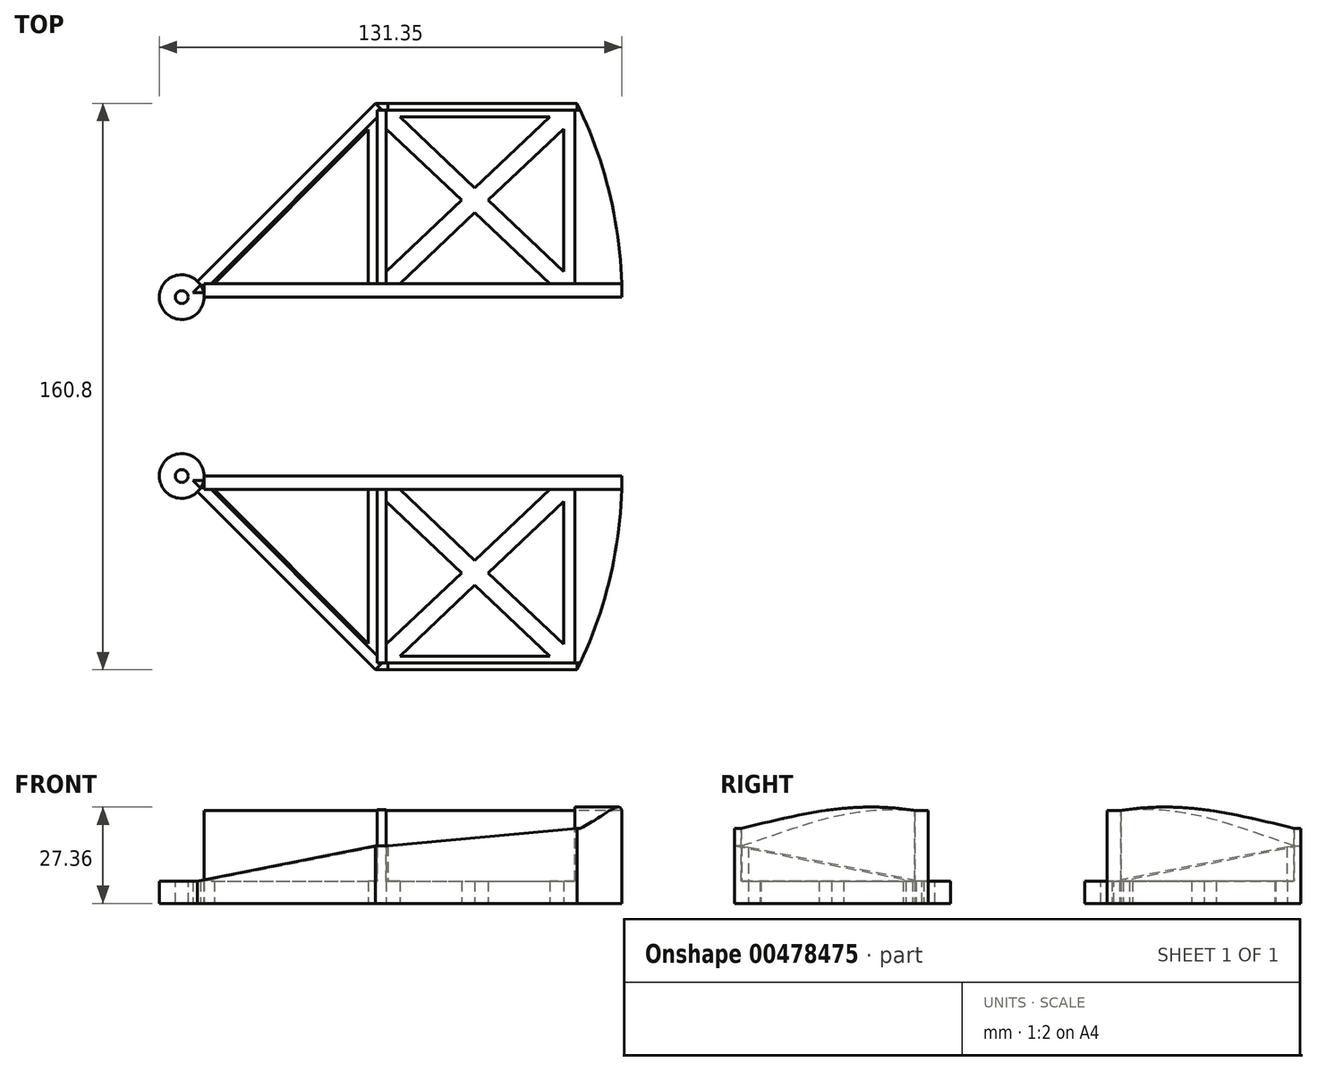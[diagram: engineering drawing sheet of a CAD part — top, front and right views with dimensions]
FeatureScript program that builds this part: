
annotation { "Feature Type Name" : "Feature", "Feature Type Description" : "" }
export const myFeature = defineFeature(function(context is Context, id is Id, definition is map)
    precondition{}
    {
        {
            var Q0;
            Q0=qCreatedBy(makeId("Top.planeOp"),FACE);
            var sketch = newSketch(context, id + "F0", { "sketchPlane" : qUnion([Q0])});
            skLineSegment(sketch, "E0", {"start": v(0, 0) * mm, "end": v(55, 55) * mm});
            skLineSegment(sketch, "E1", {"start": v(55, 55) * mm, "end": v(112.25, 55) * mm});
            skLineSegment(sketch, "E2", {"start": v(112.25, 55) * mm, "end": v(112.25, 0) * mm});
            skLineSegment(sketch, "E3", {"start": v(112.25, 0) * mm, "end": v(0, 0) * mm});
            skLineSegment(sketch, "E4.0", {"start": v(3.14, 1.3) * mm, "end": v(55.54, 53.7) * mm});
            skLineSegment(sketch, "E4.1", {"start": v(110.95, 1.3) * mm, "end": v(3.14, 1.3) * mm});
            skLineSegment(sketch, "E4.2", {"start": v(110.95, 53.7) * mm, "end": v(110.95, 1.3) * mm});
            skLineSegment(sketch, "E4.3", {"start": v(55.54, 53.7) * mm, "end": v(110.95, 53.7) * mm});
            skLineSegment(sketch, "E5", {"start": v(55.54, 53.7) * mm, "end": v(83.24, 27.5) * mm});
            skLineSegment(sketch, "E6", {"start": v(55.54, 53.7) * mm, "end": v(55.54, 1.3) * mm});
            skLineSegment(sketch, "E7", {"start": v(83.24, 27.5) * mm, "end": v(110.95, 1.3) * mm});
            skLineSegment(sketch, "E8", {"start": v(55.54, 1.3) * mm, "end": v(83.24, 27.5) * mm});
            skLineSegment(sketch, "E9", {"start": v(83.24, 27.5) * mm, "end": v(110.95, 53.7) * mm});
            skLineSegment(sketch, "E10.0", {"start": v(58.08, 47.8) * mm, "end": v(58.08, 7.2) * mm});
            skLineSegment(sketch, "E10.1", {"start": v(58.08, 47.8) * mm, "end": v(79.55, 27.5) * mm});
            skLineSegment(sketch, "E10.2", {"start": v(58.08, 7.2) * mm, "end": v(79.55, 27.5) * mm});
            skLineSegment(sketch, "E11.0", {"start": v(61.92, 51.16) * mm, "end": v(83.24, 31) * mm});
            skLineSegment(sketch, "E11.1", {"start": v(61.92, 51.16) * mm, "end": v(104.57, 51.16) * mm});
            skLineSegment(sketch, "E11.2", {"start": v(83.24, 31) * mm, "end": v(104.57, 51.16) * mm});
            skLineSegment(sketch, "E12.0", {"start": v(86.94, 27.5) * mm, "end": v(108.4, 7.2) * mm});
            skLineSegment(sketch, "E12.1", {"start": v(86.94, 27.5) * mm, "end": v(108.4, 47.8) * mm});
            skLineSegment(sketch, "E12.2", {"start": v(108.4, 47.8) * mm, "end": v(108.4, 7.2) * mm});
            skLineSegment(sketch, "E13", {"start": v(61.92, 3.84) * mm, "end": v(83.24, 24) * mm});
            skLineSegment(sketch, "E14", {"start": v(83.24, 24) * mm, "end": v(104.57, 3.84) * mm});
            skLineSegment(sketch, "E15", {"start": v(104.57, 3.84) * mm, "end": v(61.92, 3.84) * mm});
            skLineSegment(sketch, "E16", {"start": v(9.27, 3.84) * mm, "end": v(53, 47.57) * mm});
            skLineSegment(sketch, "E17", {"start": v(53, 47.57) * mm, "end": v(53, 3.84) * mm});
            skLineSegment(sketch, "E18", {"start": v(53, 3.84) * mm, "end": v(9.27, 3.84) * mm});
            skCircle(sketch, "E19", {"center": v(0, 0) * mm, "radius": 6.35 * mm});
            skCircle(sketch, "E20", {"center": v(0, 0) * mm, "radius": 125 * mm});
            skLineSegment(sketch, "E21", {"start": v(112.25, 0) * mm, "end": v(125, 0) * mm});
            skSolve(sketch);
        }
        {
            var Q0;
            {var subQ0=sQuery(id+"F0.wireOp",EDGE,"E3");var subQ1=sQuery(id+"F0.wireOp",EDGE,"E0");var subQ2=makeQuery(id+"F0.imprint","INTERSECT",VERTEX,{"derivedFrom":[subQ1,subQ0]});Q0=makeQuery(id+"F0.imprint","IMPRINT",FACE,{"disambiguationData":[TD([[makeQuery(id+"F0.imprint","IMPRINT",EDGE,{"disambiguationData":[TD([[subQ2,-1.0]])],"derivedFrom":subQ1}),1.0]])]});}
            var Q1;
            {var subQ6=sQuery(id+"F0.wireOp",EDGE,"E3");var subQ7=sQuery(id+"F0.wireOp",EDGE,"E0");var subQ8=makeQuery(id+"F0.imprint","INTERSECT",VERTEX,{"derivedFrom":[subQ7,subQ6]});Q1=makeQuery(id+"F0.imprint","IMPRINT",FACE,{"disambiguationData":[TD([[makeQuery(id+"F0.imprint","IMPRINT",EDGE,{"disambiguationData":[TD([[subQ8,-1.0]])],"derivedFrom":subQ7}),-1.0]])]});}
            var Q2;
            {var subQ13=sQuery(id+"F0.wireOp",EDGE,"E1");Q2=makeQuery(id+"F0.imprint","IMPRINT",FACE,{"disambiguationData":[TD([[makeQuery(id+"F0.imprint","IMPRINT",EDGE,{"derivedFrom":subQ13}),-1.0]])]});}
            var Q3;
            {var subQ0=sQuery(id+"F0.wireOp",EDGE,"E6");Q3=makeQuery(id+"F0.imprint","IMPRINT",FACE,{"disambiguationData":[TD([[makeQuery(id+"F0.imprint","IMPRINT",EDGE,{"derivedFrom":subQ0}),-1.0]])]});}
            var Q4;
            Q4=makeQuery(id+"F0.imprint","IMPRINT",FACE,{"disambiguationData":[TD([[makeQuery(id+"F0.imprint","IMPRINT",EDGE,{"derivedFrom":sQuery(id+"F0.wireOp",EDGE,"E5")}),-1.0]])]});
            var Q5;
            {var subQ1=sQuery(id+"F0.wireOp",EDGE,"E7");Q5=makeQuery(id+"F0.imprint","IMPRINT",FACE,{"disambiguationData":[TD([[makeQuery(id+"F0.imprint","IMPRINT",EDGE,{"derivedFrom":subQ1}),-1.0]])]});}
            var Q6;
            Q6=makeQuery(id+"F0.imprint","IMPRINT",FACE,{"disambiguationData":[TD([[makeQuery(id+"F0.imprint","IMPRINT",EDGE,{"derivedFrom":sQuery(id+"F0.wireOp",EDGE,"E4.3")}),-1.0]])]});
            var Q7;
            Q7=makeQuery(id+"F0.imprint","IMPRINT",FACE,{"disambiguationData":[TD([[makeQuery(id+"F0.imprint","IMPRINT",EDGE,{"derivedFrom":sQuery(id+"F0.wireOp",EDGE,"E4.2")}),-1.0]])]});
            var Q8;
            {var subQ0=sQuery(id+"F0.wireOp",EDGE,"E2");Q8=makeQuery(id+"F0.imprint","IMPRINT",FACE,{"disambiguationData":[TD([[makeQuery(id+"F0.imprint","IMPRINT",EDGE,{"derivedFrom":subQ0}),1.0]])]});}
            extrude(context, id + "F1", {"entities" : qUnion([Q0, Q1, Q2, Q3, Q4, Q5, Q6, Q7, Q8]), "depth" : 6.35 * mm});
        }
        {
            var Q0;
            Q0=makeQuery(id+"F1.opExtrude","CAP_FACE",FACE,{"disambiguationData":[OSD([sQuery(id+"F0.wireOp",EDGE,"E0"),sQuery(id+"F0.wireOp",EDGE,"E1"),sQuery(id+"F0.wireOp",EDGE,"E2"),sQuery(id+"F0.wireOp",EDGE,"E3"),sQuery(id+"F0.wireOp",EDGE,"E10.0"),sQuery(id+"F0.wireOp",EDGE,"E10.1"),sQuery(id+"F0.wireOp",EDGE,"E10.2"),sQuery(id+"F0.wireOp",EDGE,"E11.0"),sQuery(id+"F0.wireOp",EDGE,"E11.1"),sQuery(id+"F0.wireOp",EDGE,"E11.2"),sQuery(id+"F0.wireOp",EDGE,"E12.0"),sQuery(id+"F0.wireOp",EDGE,"E12.1"),sQuery(id+"F0.wireOp",EDGE,"E12.2"),sQuery(id+"F0.wireOp",EDGE,"E13"),sQuery(id+"F0.wireOp",EDGE,"E14"),sQuery(id+"F0.wireOp",EDGE,"E15"),sQuery(id+"F0.wireOp",EDGE,"E16"),sQuery(id+"F0.wireOp",EDGE,"E17"),sQuery(id+"F0.wireOp",EDGE,"E18"),sQuery(id+"F0.wireOp",EDGE,"E19")])],"isStart":false});
            var sketch = newSketch(context, id + "F2", { "sketchPlane" : qUnion([Q0])});
            skCircle(sketch, "E22", {"center": v(0, 0) * mm, "radius": 1.84 * mm});
            skSolve(sketch);
        }
        {
            var Q0;
            Q0=qSketchRegion(id+"F2",true);
            extrude(context, id + "F3", {"entities" : qUnion([Q0]), "operationType" : NewBodyOperationType.REMOVE, "oppositeDirection" : true, "depth" : 25.4 * mm});
        }
        {
            var Q0;
            Q0=makeQuery(id+"F1.opExtrude","CAP_FACE",FACE,{"disambiguationData":[OSD([sQuery(id+"F0.wireOp",EDGE,"E0"),sQuery(id+"F0.wireOp",EDGE,"E1"),sQuery(id+"F0.wireOp",EDGE,"E2"),sQuery(id+"F0.wireOp",EDGE,"E3"),sQuery(id+"F0.wireOp",EDGE,"E10.0"),sQuery(id+"F0.wireOp",EDGE,"E10.1"),sQuery(id+"F0.wireOp",EDGE,"E10.2"),sQuery(id+"F0.wireOp",EDGE,"E11.0"),sQuery(id+"F0.wireOp",EDGE,"E11.1"),sQuery(id+"F0.wireOp",EDGE,"E11.2"),sQuery(id+"F0.wireOp",EDGE,"E12.0"),sQuery(id+"F0.wireOp",EDGE,"E12.1"),sQuery(id+"F0.wireOp",EDGE,"E12.2"),sQuery(id+"F0.wireOp",EDGE,"E13"),sQuery(id+"F0.wireOp",EDGE,"E14"),sQuery(id+"F0.wireOp",EDGE,"E15"),sQuery(id+"F0.wireOp",EDGE,"E16"),sQuery(id+"F0.wireOp",EDGE,"E17"),sQuery(id+"F0.wireOp",EDGE,"E18"),sQuery(id+"F0.wireOp",EDGE,"E19")])],"isStart":false});
            var sketch = newSketch(context, id + "F4", { "sketchPlane" : qUnion([Q0])});
            skLineSegment(sketch, "E23.bottom", {"start": v(9.27, 0) * mm, "end": v(6.35, 0) * mm});
            skLineSegment(sketch, "E23.top", {"start": v(9.27, 3.84) * mm, "end": v(6.35, 3.84) * mm});
            skLineSegment(sketch, "E23.left", {"start": v(6.35, 0) * mm, "end": v(6.35, 3.84) * mm});
            skLineSegment(sketch, "E23.right", {"start": v(9.27, 0) * mm, "end": v(9.27, 3.84) * mm});
            skSolve(sketch);
        }
        {
            var Q0;
            Q0=qSketchRegion(id+"F4",true);
            extrude(context, id + "F5", {"entities" : qUnion([Q0]), "operationType" : NewBodyOperationType.ADD, "depth" : 20 * mm});
        }
        {
            var Q0;
            Q0=makeQuery(id+"F1.opExtrude","SWEPT_FACE",FACE,{"disambiguationData":[OSD([sQuery(id+"F0.wireOp",EDGE,"E0")])]});
            var sketch = newSketch(context, id + "F6", { "sketchPlane" : qUnion([Q0])});
            skLineSegment(sketch, "E24", {"start": v(-77.78, 6.35) * mm, "end": v(-77.78, 16.35) * mm});
            skLineSegment(sketch, "E25", {"start": v(-77.78, 16.35) * mm, "end": v(-6.35, 6.35) * mm});
            skLineSegment(sketch, "E26", {"start": v(-6.35, 6.35) * mm, "end": v(-77.78, 6.35) * mm});
            skSolve(sketch);
        }
        {
            var Q0;
            Q0=qSketchRegion(id+"F6",true);
            var Q1;
            Q1=makeQuery(id+"F1.opExtrude","SWEPT_FACE",FACE,{"disambiguationData":[OSD([sQuery(id+"F0.wireOp",EDGE,"E16")])]});
            extrude(context, id + "F7", {"entities" : qUnion([Q0]), "operationType" : NewBodyOperationType.ADD, "oppositeDirection" : true, "endBoundEntityFace" : qUnion([Q1]), "depth" : 3.17 * mm});
        }
        {
            var Q0;
            Q0=makeQuery(id+"F1.opExtrude","SWEPT_FACE",FACE,{"disambiguationData":[OSD([sQuery(id+"F0.wireOp",EDGE,"E1")])]});
            var sketch = newSketch(context, id + "F8", { "sketchPlane" : qUnion([Q0])});
            skLineSegment(sketch, "E27", {"start": v(-112.25, 6.35) * mm, "end": v(-112.25, 21.35) * mm});
            skLineSegment(sketch, "E28", {"start": v(-112.25, 21.35) * mm, "end": v(-58.52, 16.35) * mm});
            skLineSegment(sketch, "E29", {"start": v(-58.52, 16.35) * mm, "end": v(-58.52, 6.35) * mm});
            skSolve(sketch);
        }
        {
            var Q0;
            {var subQ0=sQuery(id+"F8.wireOp",EDGE,"E27");Q0=makeQuery(id+"F8.imprint","IMPRINT",FACE,{"disambiguationData":[TD([[makeQuery(id+"F8.imprint","IMPRINT",EDGE,{"derivedFrom":subQ0}),-1.0]])]});}
            extrude(context, id + "F9", {"entities" : qUnion([Q0]), "operationType" : NewBodyOperationType.ADD, "oppositeDirection" : true, "depth" : 1.9 * mm});
        }
        {
            var Q1;
            Q1=makeQuery(id+"F7.opExtrude","SWEPT_FACE",FACE,{"disambiguationData":[OSD([sQuery(id+"F6.wireOp",EDGE,"E24")])]});
            var Q2;
            Q2=makeQuery(id+"F9.opExtrude","SWEPT_FACE",FACE,{"disambiguationData":[OSD([sQuery(id+"F8.wireOp",EDGE,"E29")])]});
            loft(context, id + "F10", {"operationType" : NewBodyOperationType.ADD, "sheetProfilesArray" : [{ "sheetProfileEntities" : qUnion([Q1]) }, { "sheetProfileEntities" : qUnion([Q2]) }]});
        }
        {
            var Q0;
            Q0=makeQuery(id+"F1.opExtrude","SWEPT_FACE",FACE,{"disambiguationData":[OSD([sQuery(id+"F0.wireOp",EDGE,"E10.0")])]});
            var sketch = newSketch(context, id + "F11", { "sketchPlane" : qUnion([Q0])});
            skLineSegment(sketch, "E30.0.0", {"start": v(0, 24.38) * mm, "end": v(0, 6.35) * mm});
            skFitSpline(sketch, "E30.0.1", {"points": [v(0, 24.38) * mm, v(1.99, 25.62) * mm, v(2.56, 26) * mm, v(3.84, 26.35) * mm]});
            skLineSegment(sketch, "E30.0.2", {"start": v(3.84, 6.35) * mm, "end": v(3.84, 26.35) * mm});
            skLineSegment(sketch, "E30.0.3", {"start": v(0, 6.35) * mm, "end": v(3.84, 6.35) * mm});
            skLineSegment(sketch, "E31.0.0", {"start": v(53.1, 21.18) * mm, "end": v(53.1, 21.35) * mm});
            skLineSegment(sketch, "E31.0.3", {"start": v(55, 16.35) * mm, "end": v(53.1, 16.35) * mm});
            skLineSegment(sketch, "E31.0.4", {"start": v(53.1, 16.35) * mm, "end": v(53.1, 21.18) * mm});
            skLineSegment(sketch, "E32", {"start": v(53.1, 16.35) * mm, "end": v(53.1, 6.35) * mm});
            skLineSegment(sketch, "E33", {"start": v(3.84, 6.35) * mm, "end": v(53.1, 6.35) * mm});
            skFitSpline(sketch, "E34", {"points": [v(53.1, 16.35) * mm, v(3.84, 26.35) * mm], "startDerivative": vector(-52.9, 16.95) * mm, "endDerivative": vector(-57.88, -5.03) * mm});
            skSolve(sketch);
        }
        {
            var Q0;
            {var subQ0=sQuery(id+"F11.wireOp",EDGE,"E32");Q0=makeQuery(id+"F11.imprint","IMPRINT",FACE,{"disambiguationData":[TD([[makeQuery(id+"F11.imprint","IMPRINT",EDGE,{"derivedFrom":subQ0}),-1.0]])]});}
            extrude(context, id + "F12", {"entities" : qUnion([Q0]), "operationType" : NewBodyOperationType.ADD, "oppositeDirection" : true, "depth" : 2.54 * mm});
        }
        {
            var Q0;
            Q0=makeQuery(id+"F5.boolean.opBoolean","MERGE",FACE,{"derivedFrom":[makeQuery(id+"F1.opExtrude","SWEPT_FACE",FACE,{"disambiguationData":[OSD([sQuery(id+"F0.wireOp",EDGE,"E3")])]}),makeQuery(id+"F5.opExtrude","SWEPT_FACE",FACE,{"disambiguationData":[OSD([sQuery(id+"F4.wireOp",EDGE,"E23.bottom")])]})]});
            cPlane(context, id + "F13", {"entities" : qUnion([Q0]), "cplaneType" : CPlaneType.OFFSET, "offset" : 25.4 * mm, "width" : 152.4 * mm, "height" : 152.4 * mm});
        }
        {
            var Q0;
            Q0=makeQuery(id+"F1.opExtrude","SWEPT_BODY",BODY,{"disambiguationData":[OSD([sQuery(id+"F0.wireOp",EDGE,"E0"),sQuery(id+"F0.wireOp",EDGE,"E1"),sQuery(id+"F0.wireOp",EDGE,"E2"),sQuery(id+"F0.wireOp",EDGE,"E3"),sQuery(id+"F0.wireOp",EDGE,"E10.0"),sQuery(id+"F0.wireOp",EDGE,"E10.1"),sQuery(id+"F0.wireOp",EDGE,"E10.2"),sQuery(id+"F0.wireOp",EDGE,"E11.0"),sQuery(id+"F0.wireOp",EDGE,"E11.1"),sQuery(id+"F0.wireOp",EDGE,"E11.2"),sQuery(id+"F0.wireOp",EDGE,"E12.0"),sQuery(id+"F0.wireOp",EDGE,"E12.1"),sQuery(id+"F0.wireOp",EDGE,"E12.2"),sQuery(id+"F0.wireOp",EDGE,"E13"),sQuery(id+"F0.wireOp",EDGE,"E14"),sQuery(id+"F0.wireOp",EDGE,"E15"),sQuery(id+"F0.wireOp",EDGE,"E16"),sQuery(id+"F0.wireOp",EDGE,"E17"),sQuery(id+"F0.wireOp",EDGE,"E18"),sQuery(id+"F0.wireOp",EDGE,"E19")])]});
            var Q1;
            Q1=qCreatedBy(id+"F13.planeOp",FACE);
            mirror(context, id + "F14", {"entities" : qUnion([Q0]), "mirrorPlane" : qUnion([Q1])});
        }
        {
            var Q0;
            Q0=makeQuery(id+"F5.opExtrude","SWEPT_FACE",FACE,{"disambiguationData":[OSD([sQuery(id+"F4.wireOp",EDGE,"E23.right")])]});
            var sketch = newSketch(context, id + "F15", { "sketchPlane" : qUnion([Q0])});
            skPoint(sketch, "E35.0", {"position": v(0, 26.35) * mm});
            skLineSegment(sketch, "E36.bottom", {"start": v(0, 26.35) * mm, "end": v(3.84, 26.35) * mm});
            skLineSegment(sketch, "E36.top", {"start": v(0, 6.35) * mm, "end": v(3.84, 6.35) * mm});
            skLineSegment(sketch, "E36.left", {"start": v(0, 26.35) * mm, "end": v(0, 6.35) * mm});
            skLineSegment(sketch, "E36.right", {"start": v(3.84, 26.35) * mm, "end": v(3.84, 6.35) * mm});
            skSolve(sketch);
        }
        {
            var Q0;
            Q0=qSketchRegion(id+"F15",true);
            var Q1;
            Q1=makeQuery(id+"F1.opExtrude","SWEPT_FACE",FACE,{"disambiguationData":[OSD([sQuery(id+"F0.wireOp",EDGE,"E20")])]});
            extrude(context, id + "F16", {"entities" : qUnion([Q0]), "operationType" : NewBodyOperationType.ADD, "endBound" : BoundingType.UP_TO_SURFACE, "endBoundEntityFace" : qUnion([Q1]), "depth" : 25.4 * mm});
        }
        {
            var Q0;
            {var subQ0=sQuery(id+"F0.wireOp",EDGE,"E20");var subQ1=sQuery(id+"F0.wireOp",EDGE,"E18");var subQ2=sQuery(id+"F0.wireOp",EDGE,"E17");var subQ3=sQuery(id+"F0.wireOp",EDGE,"E16");var subQ4=sQuery(id+"F0.wireOp",EDGE,"E15");var subQ5=sQuery(id+"F0.wireOp",EDGE,"E14");var subQ6=sQuery(id+"F0.wireOp",EDGE,"E13");var subQ7=sQuery(id+"F0.wireOp",EDGE,"E12.2");var subQ8=sQuery(id+"F0.wireOp",EDGE,"E12.1");var subQ9=sQuery(id+"F0.wireOp",EDGE,"E10.0");var subQ10=sQuery(id+"F0.wireOp",EDGE,"E21");var subQ11=sQuery(id+"F0.wireOp",EDGE,"E3");var subQ12=sQuery(id+"F0.wireOp",EDGE,"E1");var subQ13=sQuery(id+"F0.wireOp",EDGE,"E0");var subQ14=sQuery(id+"F0.wireOp",EDGE,"E11.1");var subQ15=sQuery(id+"F0.wireOp",EDGE,"E10.1");var subQ16=sQuery(id+"F0.wireOp",EDGE,"E10.2");var subQ17=sQuery(id+"F0.wireOp",EDGE,"E11.0");var subQ18=sQuery(id+"F0.wireOp",EDGE,"E11.2");var subQ19=sQuery(id+"F0.wireOp",EDGE,"E12.0");Q0=makeQuery(id+"F14.opPattern","COPY",FACE,{"derivedFrom":makeQuery(id+"F7.boolean.opBoolean","SPLIT",FACE,{"disambiguationData":[TD([makeQuery(id+"F1.opExtrude","SWEPT_FACE",FACE,{"disambiguationData":[OSD([subQ12])]})])],"derivedFrom":makeQuery(id+"F1.opExtrude","CAP_FACE",FACE,{"disambiguationData":[OSD([subQ13,subQ12,subQ11,sQuery(id+"F0.wireOp",EDGE,"E4.0"),sQuery(id+"F0.wireOp",EDGE,"E4.1"),subQ9,subQ15,subQ16,subQ17,subQ14,subQ18,subQ19,subQ8,subQ7,subQ6,subQ5,subQ4,subQ3,subQ2,subQ1,sQuery(id+"F0.wireOp",EDGE,"E19"),subQ0,subQ10])],"isStart":false})}),"instanceName":"1"});}
            var sketch = newSketch(context, id + "F17", { "sketchPlane" : qUnion([Q0])});
            skLineSegment(sketch, "E37", {"start": v(112.25, -103.9) * mm, "end": v(113.16, -103.9) * mm});
            skLineSegment(sketch, "E38.0.0", {"start": v(58.08, -54.64) * mm, "end": v(58.08, -58) * mm});
            skLineSegment(sketch, "E38.0.1", {"start": v(58.08, -58) * mm, "end": v(79.55, -78.3) * mm});
            skLineSegment(sketch, "E38.0.2", {"start": v(79.55, -78.3) * mm, "end": v(58.08, -98.6) * mm});
            skLineSegment(sketch, "E38.0.3", {"start": v(58.08, -98.6) * mm, "end": v(58.08, -103.78) * mm});
            skLineSegment(sketch, "E38.0.4", {"start": v(58.08, -103.78) * mm, "end": v(58.52, -103.9) * mm});
            skLineSegment(sketch, "E38.0.5", {"start": v(58.52, -103.9) * mm, "end": v(112.25, -103.9) * mm});
            skLineSegment(sketch, "E38.0.6", {"start": v(112.25, -103.9) * mm, "end": v(112.25, -105.8) * mm});
            skArc(sketch, "E38.0.7", {"start": v(112.25, -105.8) * mm, "mid": v(121.77, -79.03) * mm, "end": v(125, -50.8) * mm});
            skLineSegment(sketch, "E38.0.8", {"start": v(125, -50.8) * mm, "end": v(9.27, -50.8) * mm});
            skLineSegment(sketch, "E38.0.9", {"start": v(9.27, -50.8) * mm, "end": v(9.27, -54.64) * mm});
            skLineSegment(sketch, "E38.0.10", {"start": v(9.27, -54.64) * mm, "end": v(53, -54.64) * mm});
            skLineSegment(sketch, "E38.0.11", {"start": v(53, -54.64) * mm, "end": v(53, -98.37) * mm});
            skLineSegment(sketch, "E38.0.12", {"start": v(53, -98.37) * mm, "end": v(9.27, -54.64) * mm});
            skLineSegment(sketch, "E38.0.13", {"start": v(9.27, -54.64) * mm, "end": v(8.33, -54.64) * mm});
            skLineSegment(sketch, "E38.0.14", {"start": v(8.33, -54.64) * mm, "end": v(55.54, -101.85) * mm});
            skLineSegment(sketch, "E38.0.15", {"start": v(55.54, -101.85) * mm, "end": v(55.54, -54.64) * mm});
            skLineSegment(sketch, "E38.0.16", {"start": v(55.54, -54.64) * mm, "end": v(58.08, -54.64) * mm});
            skSolve(sketch);
        }
        {
            var Q0;
            {var subQ0=sQuery(id+"F17.wireOp",EDGE,"E37");Q0=makeQuery(id+"F17.imprint","IMPRINT",FACE,{"disambiguationData":[TD([[makeQuery(id+"F17.imprint","IMPRINT",EDGE,{"derivedFrom":subQ0}),-1.0]])]});}
            var Q1;
            Q1=makeQuery(id+"F14.opPattern","COPY",VERTEX,{"derivedFrom":makeQuery(id+"F9.opExtrude","CAP_VERTEX",VERTEX,{"disambiguationData":[OSD([sQuery(id+"F8.wireOp",EDGE,"E27"),sQuery(id+"F8.wireOp",EDGE,"E28")])],"isStart":true}),"instanceName":"1"});
            extrude(context, id + "F18", {"entities" : qUnion([Q0]), "operationType" : NewBodyOperationType.ADD, "endBound" : BoundingType.UP_TO_VERTEX, "endBoundEntityVertex" : qUnion([Q1]), "depth" : 25.4 * mm});
        }
        {
            var Q0;
            Q0=makeQuery(id+"F14.opPattern","COPY",FACE,{"derivedFrom":makeQuery(id+"F1.opExtrude","SWEPT_FACE",FACE,{"disambiguationData":[OSD([sQuery(id+"F0.wireOp",EDGE,"E12.2")])]}),"instanceName":"1"});
            cPlane(context, id + "F19", {"entities" : qUnion([Q0]), "cplaneType" : CPlaneType.OFFSET, "offset" : 3.17 * mm, "oppositeDirection" : true, "width" : 152.4 * mm, "height" : 152.4 * mm});
        }
        {
            var Q0;
            Q0=qCreatedBy(id+"F19.planeOp",FACE);
            var sketch = newSketch(context, id + "F20", { "sketchPlane" : qUnion([Q0])});
            skLineSegment(sketch, "E39.0.0", {"start": v(105.8, 0) * mm, "end": v(50.8, 0) * mm});
            skLineSegment(sketch, "E39.0.1", {"start": v(50.8, 0) * mm, "end": v(50.8, 6.35) * mm});
            skLineSegment(sketch, "E39.0.2", {"start": v(50.8, 6.35) * mm, "end": v(103.9, 6.35) * mm});
            skLineSegment(sketch, "E39.0.3", {"start": v(103.9, 6.35) * mm, "end": v(103.9, 21.35) * mm});
            skLineSegment(sketch, "E39.0.4", {"start": v(103.9, 21.35) * mm, "end": v(105.8, 21.35) * mm});
            skLineSegment(sketch, "E39.0.5", {"start": v(105.8, 21.35) * mm, "end": v(105.8, 0) * mm});
            skLineSegment(sketch, "E40.0", {"start": v(54.64, 6.35) * mm, "end": v(54.64, 26.35) * mm});
            skFitSpline(sketch, "E41", {"points": [v(103.9, 21.35) * mm, v(54.64, 26.35) * mm], "startDerivative": vector(-47.91, 11.07) * mm, "endDerivative": vector(-54.43, -9.01) * mm});
            skSolve(sketch);
        }
        {
            var Q0;
            {var subQ0=sQuery(id+"F20.wireOp",EDGE,"E39.0.3");Q0=makeQuery(id+"F20.imprint","IMPRINT",FACE,{"disambiguationData":[TD([[makeQuery(id+"F20.imprint","IMPRINT",EDGE,{"derivedFrom":subQ0}),1.0]])]});}
            var Q1;
            Q1=makeQuery(id+"F18.boolean.opBoolean","MERGE",FACE,{"derivedFrom":[makeQuery(id+"F14.opPattern","COPY",FACE,{"derivedFrom":makeQuery(id+"F1.opExtrude","SWEPT_FACE",FACE,{"disambiguationData":[OSD([sQuery(id+"F0.wireOp",EDGE,"E20")])]}),"instanceName":"1"}),makeQuery(id+"F18.opExtrude","SWEPT_FACE",FACE,{"disambiguationData":[OSD([sQuery(id+"F17.wireOp",EDGE,"E38.0.7")])]})]});
            extrude(context, id + "F21", {"entities" : qUnion([Q0]), "operationType" : NewBodyOperationType.ADD, "endBound" : BoundingType.UP_TO_SURFACE, "oppositeDirection" : true, "endBoundEntityFace" : qUnion([Q1]), "depth" : 25.4 * mm});
        }
        {
            var Q0;
            Q0=makeQuery(id+"F14.opPattern","COPY",FACE,{"derivedFrom":makeQuery(id+"F5.opExtrude","SWEPT_FACE",FACE,{"disambiguationData":[OSD([sQuery(id+"F4.wireOp",EDGE,"E23.right")])]}),"instanceName":"1"});
            var sketch = newSketch(context, id + "F22", { "sketchPlane" : qUnion([Q0])});
            skLineSegment(sketch, "E42.bottom", {"start": v(-54.64, 26.35) * mm, "end": v(-50.8, 26.35) * mm});
            skLineSegment(sketch, "E42.top", {"start": v(-54.64, 6.35) * mm, "end": v(-50.8, 6.35) * mm});
            skLineSegment(sketch, "E42.left", {"start": v(-54.64, 26.35) * mm, "end": v(-54.64, 6.35) * mm});
            skLineSegment(sketch, "E42.right", {"start": v(-50.8, 26.35) * mm, "end": v(-50.8, 6.35) * mm});
            skSolve(sketch);
        }
        {
            var Q0;
            Q0=qSketchRegion(id+"F22",true);
            var Q1;
            {var subQ0=sQuery(id+"F17.wireOp",EDGE,"E38.0.7");var subQ1=sQuery(id+"F0.wireOp",EDGE,"E20");Q1=makeQuery(id+"F21.boolean.opBoolean","MERGE",FACE,{"derivedFrom":[makeQuery(id+"F18.boolean.opBoolean","MERGE",FACE,{"derivedFrom":[makeQuery(id+"F14.opPattern","COPY",FACE,{"derivedFrom":makeQuery(id+"F1.opExtrude","SWEPT_FACE",FACE,{"disambiguationData":[OSD([subQ1])]}),"instanceName":"1"}),makeQuery(id+"F18.opExtrude","SWEPT_FACE",FACE,{"disambiguationData":[OSD([subQ0])]})]}),makeQuery(id+"F21.opExtrude","CAP_FACE",FACE,{"disambiguationData":[OSD([subQ1,subQ0])],"isStart":false})]});}
            extrude(context, id + "F23", {"entities" : qUnion([Q0]), "operationType" : NewBodyOperationType.ADD, "endBound" : BoundingType.UP_TO_SURFACE, "endBoundEntityFace" : qUnion([Q1]), "depth" : 25.4 * mm});
        }
        {
            var Q0;
            Q0=makeQuery(id+"F14.opPattern","COPY",BODY,{"derivedFrom":makeQuery(id+"F1.opExtrude","SWEPT_BODY",BODY,{"disambiguationData":[OSD([sQuery(id+"F0.wireOp",EDGE,"E0"),sQuery(id+"F0.wireOp",EDGE,"E1"),sQuery(id+"F0.wireOp",EDGE,"E3"),sQuery(id+"F0.wireOp",EDGE,"E4.0"),sQuery(id+"F0.wireOp",EDGE,"E4.1"),sQuery(id+"F0.wireOp",EDGE,"E10.0"),sQuery(id+"F0.wireOp",EDGE,"E10.1"),sQuery(id+"F0.wireOp",EDGE,"E10.2"),sQuery(id+"F0.wireOp",EDGE,"E11.0"),sQuery(id+"F0.wireOp",EDGE,"E11.1"),sQuery(id+"F0.wireOp",EDGE,"E11.2"),sQuery(id+"F0.wireOp",EDGE,"E12.0"),sQuery(id+"F0.wireOp",EDGE,"E12.1"),sQuery(id+"F0.wireOp",EDGE,"E12.2"),sQuery(id+"F0.wireOp",EDGE,"E13"),sQuery(id+"F0.wireOp",EDGE,"E14"),sQuery(id+"F0.wireOp",EDGE,"E15"),sQuery(id+"F0.wireOp",EDGE,"E16"),sQuery(id+"F0.wireOp",EDGE,"E17"),sQuery(id+"F0.wireOp",EDGE,"E18"),sQuery(id+"F0.wireOp",EDGE,"E19"),sQuery(id+"F0.wireOp",EDGE,"E20"),sQuery(id+"F0.wireOp",EDGE,"E21")])]}),"instanceName":"1"});
            var Q1;
            Q1=qCreatedBy(id+"F13.planeOp",FACE);
            mirror(context, id + "F24", {"operationType" : NewBodyOperationType.ADD, "entities" : qUnion([Q0]), "mirrorPlane" : qUnion([Q1])});
        }
    });
